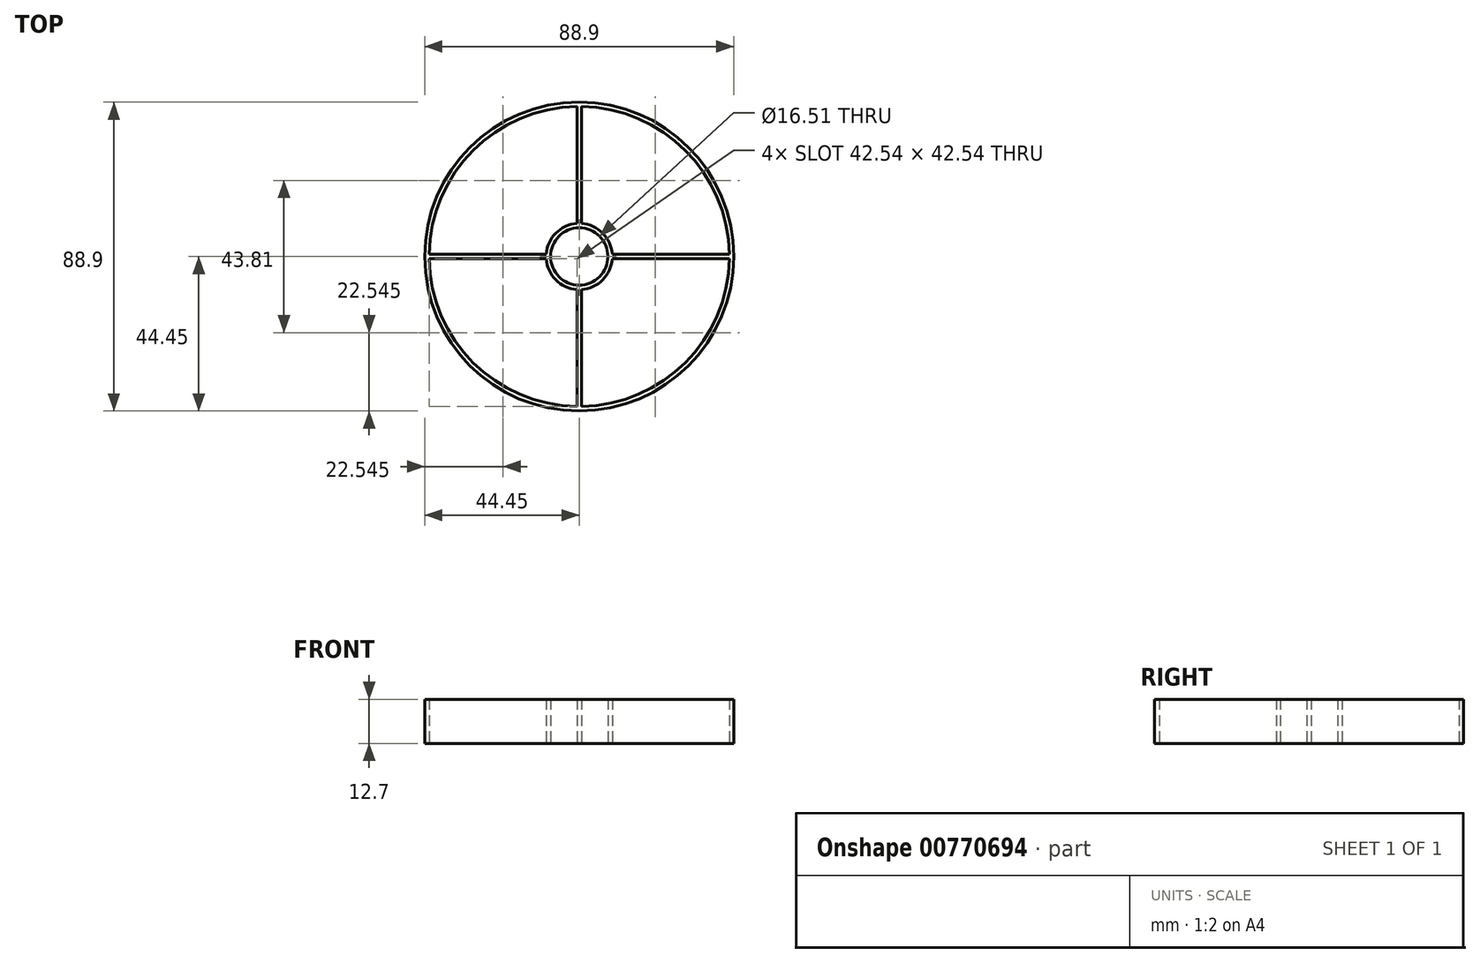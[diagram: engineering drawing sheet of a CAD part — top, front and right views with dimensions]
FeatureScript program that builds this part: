
annotation { "Feature Type Name" : "Feature", "Feature Type Description" : "" }
export const myFeature = defineFeature(function(context is Context, id is Id, definition is map)
    precondition{}
    {
        {
            var Q0;
            Q0=qCreatedBy(makeId("Top.planeOp"),FACE);
            var sketch = newSketch(context, id + "F0", { "sketchPlane" : qUnion([Q0])});
            skCircle(sketch, "E0", {"center": v(0, 0) * mm, "radius": 44.45 * mm});
            skArc(sketch, "E1", {"start": v(-0.64, 43.18) * mm, "mid": v(-30.53, 30.53) * mm, "end": v(-43.18, 0.63) * mm});
            skLineSegment(sketch, "E2", {"start": v(-44.45, 0) * mm, "end": v(44.45, 0) * mm, "construction": true});
            skLineSegment(sketch, "E3", {"start": v(-31.43, -31.43) * mm, "end": v(31.43, 31.43) * mm, "construction": true});
            skLineSegment(sketch, "E4", {"start": v(0, 44.45) * mm, "end": v(0, -44.45) * mm, "construction": true});
            skLineSegment(sketch, "E5", {"start": v(-30.53, 30.53) * mm, "end": v(30.53, -30.53) * mm, "construction": true});
            skArc(sketch, "E6", {"start": v(9.5, 0.64) * mm, "mid": v(6.74, 6.74) * mm, "end": v(0.64, 9.5) * mm});
            skCircle(sketch, "E7", {"center": v(0, 0) * mm, "radius": 8.26 * mm});
            skLineSegment(sketch, "E8", {"start": v(0.64, 9.5) * mm, "end": v(0.64, 43.18) * mm});
            skLineSegment(sketch, "E9", {"start": v(-0.64, 43.18) * mm, "end": v(-0.63, 9.5) * mm});
            skLineSegment(sketch, "E10", {"start": v(-43.18, 0.63) * mm, "end": v(-9.5, 0.63) * mm});
            skLineSegment(sketch, "E11", {"start": v(-43.18, -0.64) * mm, "end": v(-9.5, -0.64) * mm});
            skLineSegment(sketch, "E12", {"start": v(9.5, 0.64) * mm, "end": v(43.18, 0.64) * mm});
            skLineSegment(sketch, "E13", {"start": v(9.5, -0.63) * mm, "end": v(43.18, -0.63) * mm});
            skLineSegment(sketch, "E14", {"start": v(0.64, -9.5) * mm, "end": v(0.64, -43.18) * mm});
            skLineSegment(sketch, "E15", {"start": v(-0.63, -9.5) * mm, "end": v(-0.63, -43.18) * mm});
            skArc(sketch, "E16.trimOffspring", {"start": v(43.18, 0.63) * mm, "mid": v(30.53, 30.53) * mm, "end": v(0.64, 43.18) * mm});
            skArc(sketch, "E17.trimOffspring", {"start": v(0.64, -43.18) * mm, "mid": v(30.53, -30.53) * mm, "end": v(43.18, -0.64) * mm});
            skArc(sketch, "E18.trimOffspring", {"start": v(-43.18, -0.64) * mm, "mid": v(-30.53, -30.53) * mm, "end": v(-0.63, -43.18) * mm});
            skArc(sketch, "E19.trimOffspring", {"start": v(-0.63, 9.5) * mm, "mid": v(-6.74, 6.74) * mm, "end": v(-9.5, 0.63) * mm});
            skArc(sketch, "E20.trimOffspring", {"start": v(-9.5, -0.64) * mm, "mid": v(-6.74, -6.74) * mm, "end": v(-0.63, -9.5) * mm});
            skArc(sketch, "E21.trimOffspring", {"start": v(0.64, -9.5) * mm, "mid": v(6.74, -6.74) * mm, "end": v(9.5, -0.64) * mm});
            skSolve(sketch);
        }
        {
            var Q0;
            Q0=makeQuery(id+"F0.imprint","IMPRINT",FACE,{"disambiguationData":[TD([[makeQuery(id+"F0.imprint","IMPRINT",EDGE,{"derivedFrom":sQuery(id+"F0.wireOp",EDGE,"E0")}),1.0]])]});
            extrude(context, id + "F1", {"entities" : qUnion([Q0]), "depth" : 12.7 * mm, "offsetDistance" : 25.4 * mm});
        }
    });
